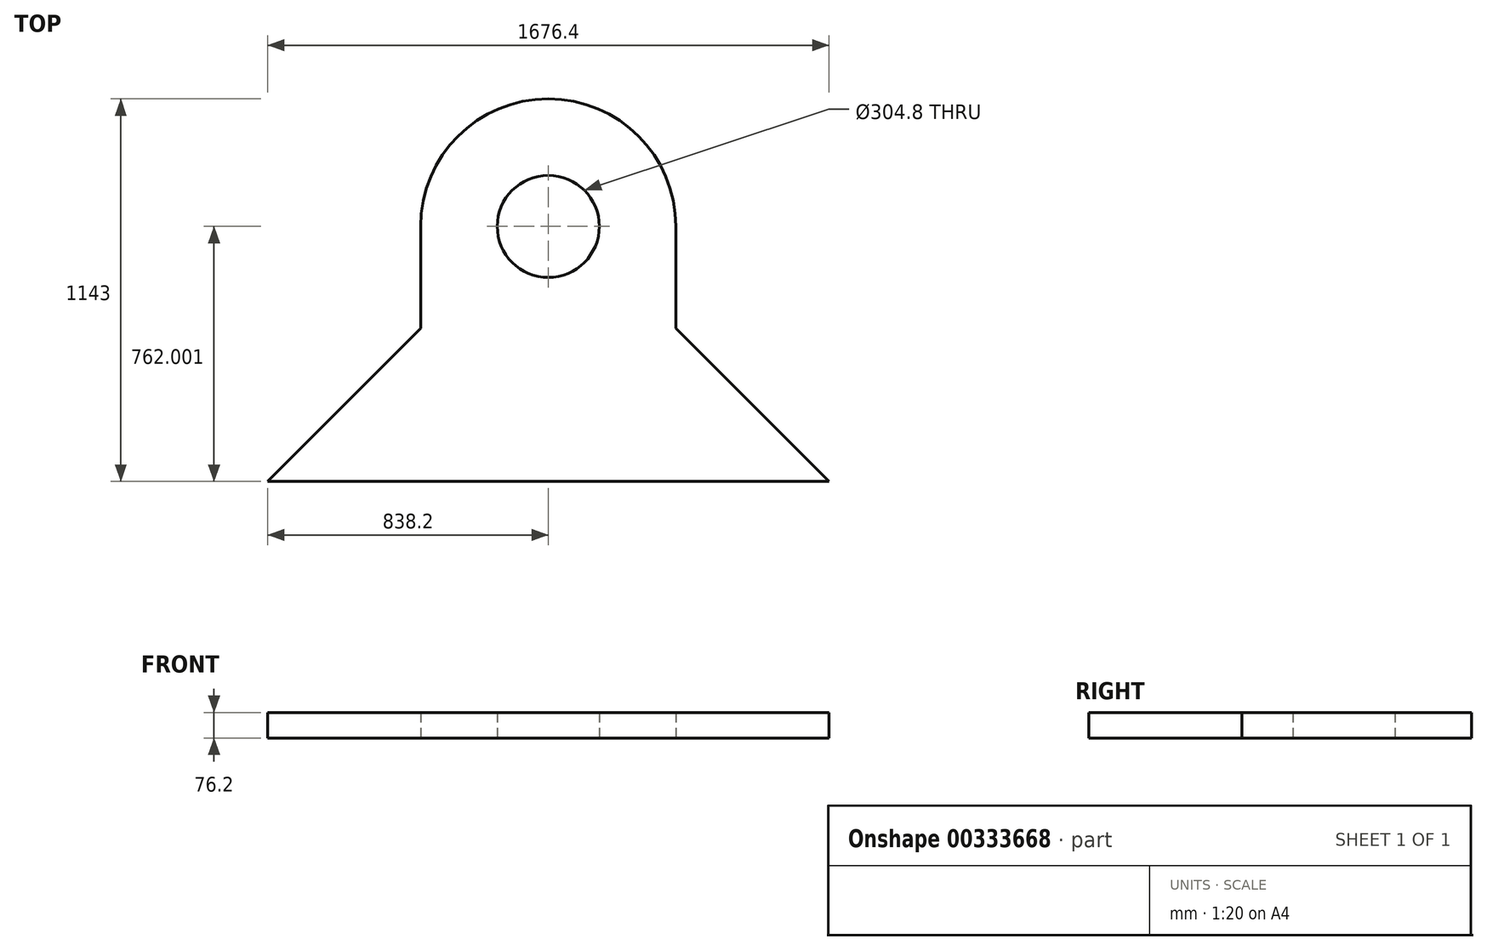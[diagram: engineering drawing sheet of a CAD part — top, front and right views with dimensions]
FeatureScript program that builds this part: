
annotation { "Feature Type Name" : "Feature", "Feature Type Description" : "" }
export const myFeature = defineFeature(function(context is Context, id is Id, definition is map)
    precondition{}
    {
        {
            var Q0;
            Q0=qCreatedBy(makeId("Top.planeOp"),FACE);
            var sketch = newSketch(context, id + "F0", { "sketchPlane" : qUnion([Q0])});
            skLineSegment(sketch, "E0", {"start": v(-838.2, -680.6) * mm, "end": v(838.2, -680.6) * mm});
            skLineSegment(sketch, "E1", {"start": v(0, 81.4) * mm, "end": v(0, -680.6) * mm, "construction": true});
            skPoint(sketch, "E1.startSnap0", {"position": v(0, -680.6) * mm});
            skPoint(sketch, "E1.endSnap0", {"position": v(0, -680.6) * mm});
            skCircle(sketch, "E2", {"center": v(0, 81.4) * mm, "radius": 152.4 * mm});
            skLineSegment(sketch, "E3", {"start": v(-838.2, -680.6) * mm, "end": v(-381, -223.4) * mm});
            skLineSegment(sketch, "E4", {"start": v(-381, -223.4) * mm, "end": v(-381, 81.4) * mm});
            skLineSegment(sketch, "E5", {"start": v(838.2, -680.6) * mm, "end": v(381, -223.4) * mm});
            skLineSegment(sketch, "E6", {"start": v(381, -223.4) * mm, "end": v(381, 81.4) * mm});
            skArc(sketch, "E7", {"start": v(381, 81.4) * mm, "mid": v(0, 462.4) * mm, "end": v(-381, 81.4) * mm});
            skSolve(sketch);
        }
        {
            var Q0;
            Q0=makeQuery(id+"F0.imprint","IMPRINT",FACE,{"disambiguationData":[TD([[makeQuery(id+"F0.imprint","IMPRINT",EDGE,{"derivedFrom":sQuery(id+"F0.wireOp",EDGE,"E0")}),1.0]])]});
            extrude(context, id + "F1", {"entities" : qUnion([Q0]), "depth" : 76.2 * mm});
        }
    });
